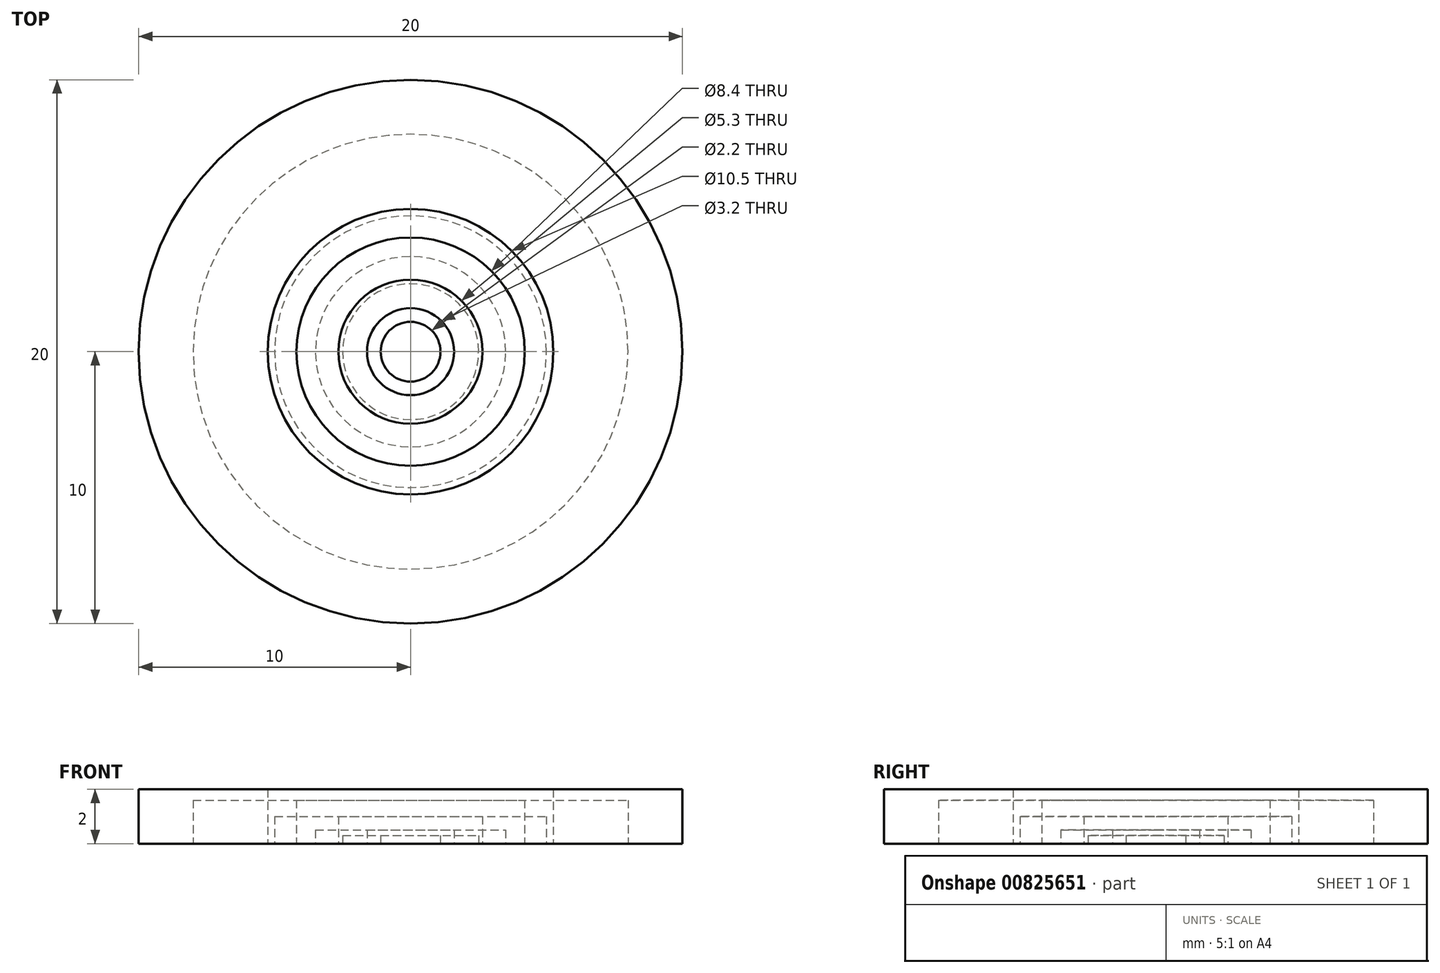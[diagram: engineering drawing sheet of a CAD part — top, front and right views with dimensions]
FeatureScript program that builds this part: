
annotation { "Feature Type Name" : "Feature", "Feature Type Description" : "" }
export const myFeature = defineFeature(function(context is Context, id is Id, definition is map)
    precondition{}
    {
        {
            var Q0;
            Q0=qCreatedBy(makeId("Front.planeOp"),FACE);
            var sketch = newSketch(context, id + "F0", { "sketchPlane" : qUnion([Q0])});
            skLineSegment(sketch, "E0.bottom", {"start": v(1.6, 0.5) * mm, "end": v(3.5, 0.5) * mm});
            skLineSegment(sketch, "E0.top", {"start": v(1.6, 0) * mm, "end": v(3.5, 0) * mm});
            skLineSegment(sketch, "E0.left", {"start": v(1.6, 0.5) * mm, "end": v(1.6, 0) * mm});
            skLineSegment(sketch, "E0.right", {"start": v(3.5, 0.5) * mm, "end": v(3.5, 0) * mm});
            skLineSegment(sketch, "E1", {"start": v(0, 0) * mm, "end": v(0, 2.48) * mm, "construction": true});
            skSolve(sketch);
        }
        {
            var Q0;
            Q0=qSketchRegion(id+"F0",true);
            var Q1;
            Q1=sQuery(id+"F0.wireOp",EDGE,"E1");
            revolve(context, id + "F1", {"entities" : qUnion([Q0]), "axis" : qUnion([Q1]), "revolveType" : RevolveType.FULL});
        }
        {
            var Q0;
            Q0=qCreatedBy(makeId("Front.planeOp"),FACE);
            var sketch = newSketch(context, id + "F2", { "sketchPlane" : qUnion([Q0])});
            skLineSegment(sketch, "E2.bottom", {"start": v(2.65, 1) * mm, "end": v(5, 1) * mm});
            skLineSegment(sketch, "E2.top", {"start": v(2.65, 0) * mm, "end": v(5, 0) * mm});
            skLineSegment(sketch, "E2.left", {"start": v(2.65, 1) * mm, "end": v(2.65, 0) * mm});
            skLineSegment(sketch, "E2.right", {"start": v(5, 1) * mm, "end": v(5, 0) * mm});
            skLineSegment(sketch, "E3", {"start": v(0, 0) * mm, "end": v(0, 3.81) * mm, "construction": true});
            skSolve(sketch);
        }
        {
            var Q0;
            Q0=qSketchRegion(id+"F2",true);
            var Q1;
            Q1=sQuery(id+"F2.wireOp",EDGE,"E3");
            revolve(context, id + "F3", {"entities" : qUnion([Q0]), "axis" : qUnion([Q1]), "revolveType" : RevolveType.FULL});
        }
        {
            var Q0;
            Q0=qCreatedBy(makeId("Front.planeOp"),FACE);
            var sketch = newSketch(context, id + "F4", { "sketchPlane" : qUnion([Q0])});
            skLineSegment(sketch, "E4", {"start": v(4.2, 0) * mm, "end": v(4.2, 1.6) * mm});
            skLineSegment(sketch, "E5", {"start": v(4.2, 1.6) * mm, "end": v(8, 1.6) * mm});
            skLineSegment(sketch, "E6", {"start": v(8, 1.6) * mm, "end": v(8, 0) * mm});
            skLineSegment(sketch, "E7", {"start": v(8, 0) * mm, "end": v(4.2, 0) * mm});
            skLineSegment(sketch, "E8", {"start": v(0, 0) * mm, "end": v(0, 2.98) * mm, "construction": true});
            skSolve(sketch);
        }
        {
            var Q0;
            Q0=qSketchRegion(id+"F4",true);
            var Q1;
            Q1=sQuery(id+"F4.wireOp",EDGE,"E8");
            revolve(context, id + "F5", {"entities" : qUnion([Q0]), "axis" : qUnion([Q1]), "revolveType" : RevolveType.FULL});
        }
        {
            var Q0;
            Q0=qCreatedBy(makeId("Front.planeOp"),FACE);
            var sketch = newSketch(context, id + "F6", { "sketchPlane" : qUnion([Q0])});
            skLineSegment(sketch, "E9.bottom", {"start": v(5.25, 0) * mm, "end": v(10, 0) * mm});
            skLineSegment(sketch, "E9.top", {"start": v(5.25, 2) * mm, "end": v(10, 2) * mm});
            skLineSegment(sketch, "E9.left", {"start": v(5.25, 0) * mm, "end": v(5.25, 2) * mm});
            skLineSegment(sketch, "E9.right", {"start": v(10, 0) * mm, "end": v(10, 2) * mm});
            skLineSegment(sketch, "E10", {"start": v(0, 0) * mm, "end": v(0, 13.9) * mm, "construction": true});
            skSolve(sketch);
        }
        {
            var Q0;
            Q0 = qSketchRegion(id + "F6", true);
            var Q1;
            Q1=sQuery(id+"F6.wireOp",EDGE,"E10");
            revolve(context, id + "F7", {"surfaceOperationType" : NewSurfaceOperationType.NEW, "entities" : qUnion([Q0]), "axis" : qUnion([Q1]), "revolveType" : RevolveType.FULL});
        }
        {
            var Q0;
            Q0=qCreatedBy(makeId("Front.planeOp"),FACE);
            var sketch = newSketch(context, id + "F8", { "sketchPlane" : qUnion([Q0])});
            skLineSegment(sketch, "E11.bottom", {"start": v(1.1, 0) * mm, "end": v(2.5, 0) * mm});
            skLineSegment(sketch, "E11.top", {"start": v(1.1, 0.3) * mm, "end": v(2.5, 0.3) * mm});
            skLineSegment(sketch, "E11.left", {"start": v(1.1, 0) * mm, "end": v(1.1, 0.3) * mm});
            skLineSegment(sketch, "E11.right", {"start": v(2.5, 0) * mm, "end": v(2.5, 0.3) * mm});
            skLineSegment(sketch, "E12", {"start": v(0, 0) * mm, "end": v(0, 0.97) * mm, "construction": true});
            skSolve(sketch);
        }
        {
            var Q0;
            Q0 = qSketchRegion(id + "F8", true);
            var Q1;
            Q1=sQuery(id+"F8.wireOp",EDGE,"E12");
            revolve(context, id + "F9", {"surfaceOperationType" : NewSurfaceOperationType.NEW, "entities" : qUnion([Q0]), "axis" : qUnion([Q1]), "revolveType" : RevolveType.FULL});
        }
    });
